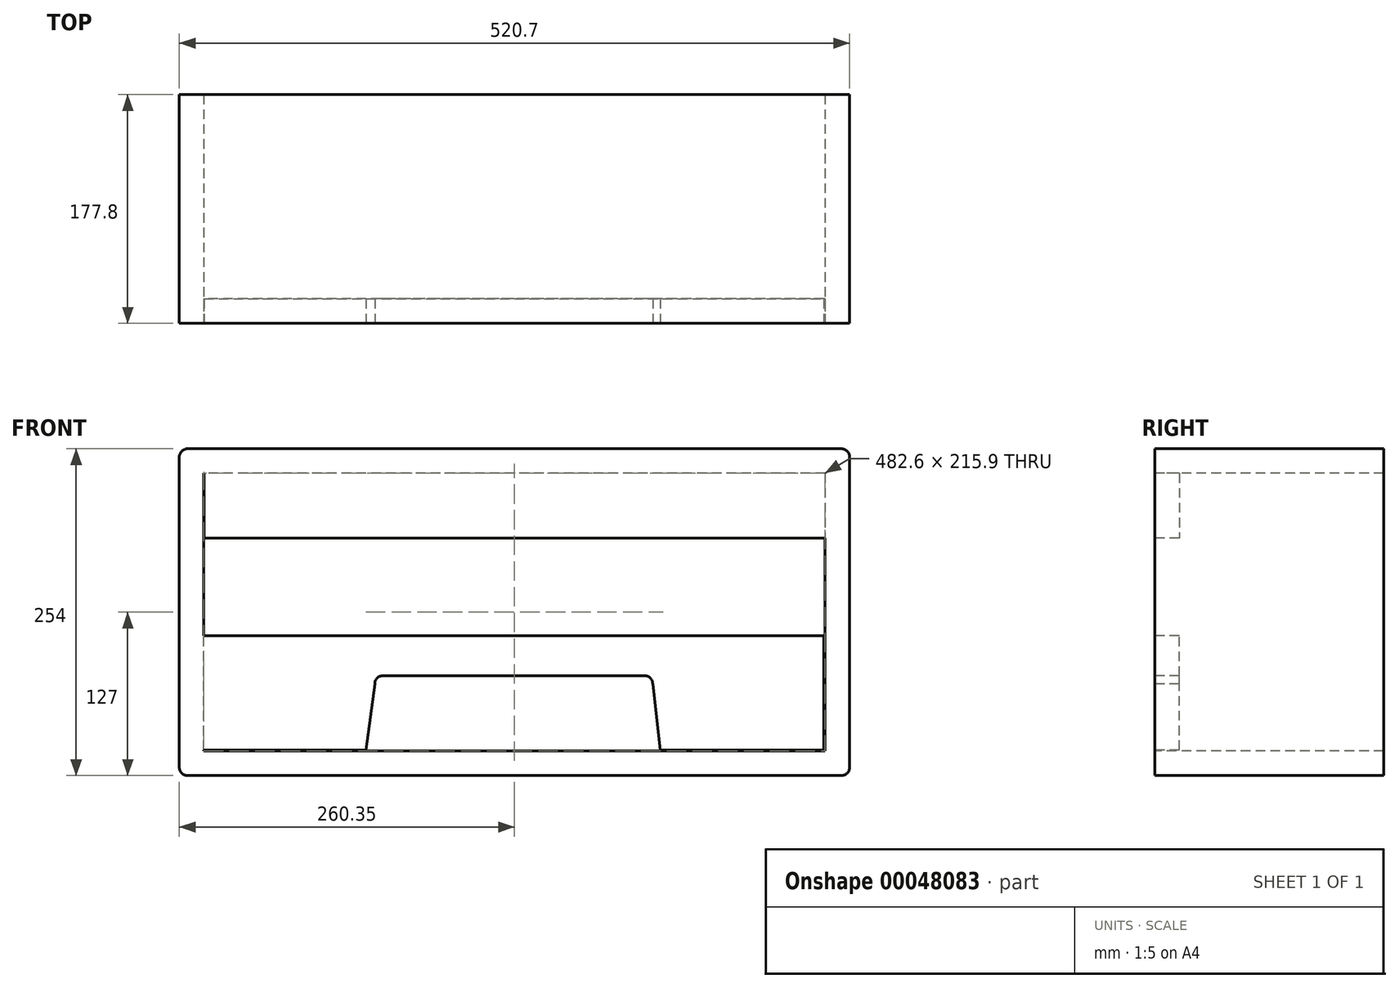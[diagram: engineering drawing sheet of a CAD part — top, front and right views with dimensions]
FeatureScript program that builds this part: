
annotation { "Feature Type Name" : "Feature", "Feature Type Description" : "" }
export const myFeature = defineFeature(function(context is Context, id is Id, definition is map)
    precondition{}
    {
        {
            var Q0;
            Q0=qCreatedBy(makeId("Front.planeOp"),FACE);
            var sketch = newSketch(context, id + "F0", { "sketchPlane" : qUnion([Q0])});
            skLineSegment(sketch, "E0.bottom", {"start": v(254, -127) * mm, "end": v(-254, -127) * mm});
            skLineSegment(sketch, "E0.top", {"start": v(254, 127) * mm, "end": v(-254, 127) * mm});
            skLineSegment(sketch, "E0.left", {"start": v(260.35, -120.65) * mm, "end": v(260.35, 120.65) * mm});
            skLineSegment(sketch, "E0.right", {"start": v(-260.35, -120.65) * mm, "end": v(-260.35, 120.65) * mm});
            skPoint(sketch, "E0.middle", {"position": v(0, 0) * mm});
            skLineSegment(sketch, "E1.bottom", {"start": v(241.3, 107.95) * mm, "end": v(-241.3, 107.95) * mm});
            skLineSegment(sketch, "E1.top", {"start": v(241.3, -107.95) * mm, "end": v(-241.3, -107.95) * mm});
            skLineSegment(sketch, "E1.left", {"start": v(241.3, 107.95) * mm, "end": v(241.3, -107.95) * mm});
            skLineSegment(sketch, "E1.right", {"start": v(-241.3, 107.95) * mm, "end": v(-241.3, -107.95) * mm});
            skPoint(sketch, "E2.center.orphan", {"position": v(38.1, -82.55) * mm});
            skPoint(sketch, "E3.center.orphan", {"position": v(95.25, -82.55) * mm});
            skPoint(sketch, "E4.center.orphan", {"position": v(146.05, -82.55) * mm});
            skPoint(sketch, "E5.center.orphan", {"position": v(203.2, -82.55) * mm});
            skPoint(sketch, "E6.top.end.orphan", {"position": v(0, -44.45) * mm});
            skPoint(sketch, "E7.visualSharp", {"position": v(-260.35, 127) * mm});
            skArc(sketch, "E7.filletArc", {"start": v(-254, 127) * mm, "mid": v(-258.5, 125.14) * mm, "end": v(-260.35, 120.65) * mm});
            skPoint(sketch, "E8.visualSharp", {"position": v(260.35, 127) * mm});
            skArc(sketch, "E8.filletArc", {"start": v(260.35, 120.65) * mm, "mid": v(258.5, 125.14) * mm, "end": v(254, 127) * mm});
            skPoint(sketch, "E9.visualSharp", {"position": v(260.35, -127) * mm});
            skArc(sketch, "E9.filletArc", {"start": v(254, -127) * mm, "mid": v(258.5, -125.14) * mm, "end": v(260.35, -120.65) * mm});
            skPoint(sketch, "E10.visualSharp", {"position": v(-260.35, -127) * mm});
            skArc(sketch, "E10.filletArc", {"start": v(-260.35, -120.65) * mm, "mid": v(-258.5, -125.14) * mm, "end": v(-254, -127) * mm});
            skLineSegment(sketch, "E11.bottom", {"start": v(-241.3, -107.95) * mm, "end": v(-222.25, -107.95) * mm});
            skLineSegment(sketch, "E11.top", {"start": v(-241.3, 107.95) * mm, "end": v(-222.25, 107.95) * mm});
            skLineSegment(sketch, "E11.left", {"start": v(-241.3, -107.95) * mm, "end": v(-241.3, 107.95) * mm});
            skLineSegment(sketch, "E11.right", {"start": v(-222.25, -107.95) * mm, "end": v(-222.25, 107.95) * mm});
            skPoint(sketch, "E6.left.end.orphan", {"position": v(241.3, -44.45) * mm});
            skLineSegment(sketch, "E12.bottom", {"start": v(241.3, -107.95) * mm, "end": v(222.25, -107.95) * mm});
            skLineSegment(sketch, "E12.top", {"start": v(241.3, 107.95) * mm, "end": v(222.25, 107.95) * mm});
            skLineSegment(sketch, "E12.left", {"start": v(241.3, -107.95) * mm, "end": v(241.3, 107.95) * mm});
            skLineSegment(sketch, "E12.right", {"start": v(222.25, -107.95) * mm, "end": v(222.25, 107.95) * mm});
            skSolve(sketch);
        }
        {
            var Q0;
            Q0=makeQuery(id+"F0.imprint","IMPRINT",FACE,{"disambiguationData":[TD([[makeQuery(id+"F0.imprint","IMPRINT",EDGE,{"derivedFrom":sQuery(id+"F0.wireOp",EDGE,"E0.bottom")}),-1.0]])]});
            var sketch = newSketch(context, id + "F1", { "sketchPlane" : qUnion([Q0])});
            skLineSegment(sketch, "E13", {"start": v(-241.05, 108.4) * mm, "end": v(-241.05, 57.6) * mm});
            skLineSegment(sketch, "E14", {"start": v(-241.05, 108.4) * mm, "end": v(241.55, 108.4) * mm});
            skLineSegment(sketch, "E15", {"start": v(241.55, 108.4) * mm, "end": v(241.55, 57.6) * mm});
            skLineSegment(sketch, "E16", {"start": v(-241.05, 57.6) * mm, "end": v(241.55, 57.6) * mm});
            skLineSegment(sketch, "E17", {"start": v(-0.55, -49.34) * mm, "end": v(-102.15, -49.34) * mm});
            skLineSegment(sketch, "E18", {"start": v(-0.55, -49.34) * mm, "end": v(101.05, -49.34) * mm});
            skPoint(sketch, "E19.start.orphan", {"position": v(0, -106.49) * mm});
            skPoint(sketch, "E20.visualSharp", {"position": v(-108.5, -49.34) * mm});
            skArc(sketch, "E20.filletArc", {"start": v(-102.15, -49.34) * mm, "mid": v(-106.64, -51.2) * mm, "end": v(-108.5, -55.69) * mm});
            skPoint(sketch, "E21.visualSharp", {"position": v(107.4, -49.34) * mm});
            skArc(sketch, "E21.filletArc", {"start": v(107.4, -55.69) * mm, "mid": v(105.54, -51.2) * mm, "end": v(101.05, -49.34) * mm});
            skLineSegment(sketch, "E22", {"start": v(240.28, -107.14) * mm, "end": v(113.28, -107.14) * mm});
            skLineSegment(sketch, "E23", {"start": v(113.28, -107.14) * mm, "end": v(107.4, -55.69) * mm});
            skLineSegment(sketch, "E24", {"start": v(-242.32, -107.14) * mm, "end": v(-115.32, -107.14) * mm});
            skLineSegment(sketch, "E25", {"start": v(-115.32, -107.14) * mm, "end": v(-108.5, -55.69) * mm});
            skPoint(sketch, "E26.end.orphan", {"position": v(-108.5, -107.14) * mm});
            skPoint(sketch, "E27.end.orphan", {"position": v(107.4, -107.14) * mm});
            skLineSegment(sketch, "E28", {"start": v(-242.32, -107.14) * mm, "end": v(-242.32, -18.24) * mm});
            skLineSegment(sketch, "E29", {"start": v(240.28, -107.14) * mm, "end": v(240.28, -18.24) * mm});
            skLineSegment(sketch, "E30", {"start": v(-242.32, -18.24) * mm, "end": v(240.28, -18.24) * mm});
            skSolve(sketch);
        }
        {
            var Q0;
            Q0 = qSketchRegion(id + "F0", true);
            extrude(context, id + "F2", {"entities" : qUnion([Q0]), "oppositeDirection" : true, "depth" : 177.8 * mm, "offsetDistance" : 25.4 * mm});
        }
        {
            var Q0;
            {var subQ4=sQuery(id+"F1.wireOp",EDGE,"jKJ7AeCj-mwpZ-X9x0-tLhN-km7y5BG7l16E");Q0=makeQuery(id+"F1.imprint","IMPRINT",FACE,{"disambiguationData":[TD([[makeQuery(id+"F1.imprint","IMPRINT",EDGE,{"derivedFrom":subQ4}),-1.0]])]});}
            var Q1;
            {var subQ0=sQuery(id+"F1.wireOp",EDGE,"E16");var subQ1=sQuery(id+"F1.wireOp",EDGE,"E13");var subQ2=makeQuery(id+"F1.imprint","INTERSECT",VERTEX,{"derivedFrom":[subQ1,subQ0]});Q1=makeQuery(id+"F1.imprint","IMPRINT",FACE,{"disambiguationData":[TD([[makeQuery(id+"F1.imprint","IMPRINT",EDGE,{"disambiguationData":[TD([[subQ2,1.0]])],"derivedFrom":subQ1}),1.0]])]});}
            extrude(context, id + "F3", {"entities" : qUnion([Q0, Q1]), "operationType" : NewBodyOperationType.ADD, "oppositeDirection" : true, "depth" : 19.05 * mm, "offsetDistance" : 25.4 * mm});
        }
        {
            var Q0;
            Q0 = qSketchRegion(id + "F1", true);
            extrude(context, id + "F4", {"entities" : qUnion([Q0]), "operationType" : NewBodyOperationType.ADD, "oppositeDirection" : true, "depth" : 19.05 * mm, "offsetDistance" : 25.4 * mm});
        }
    });
